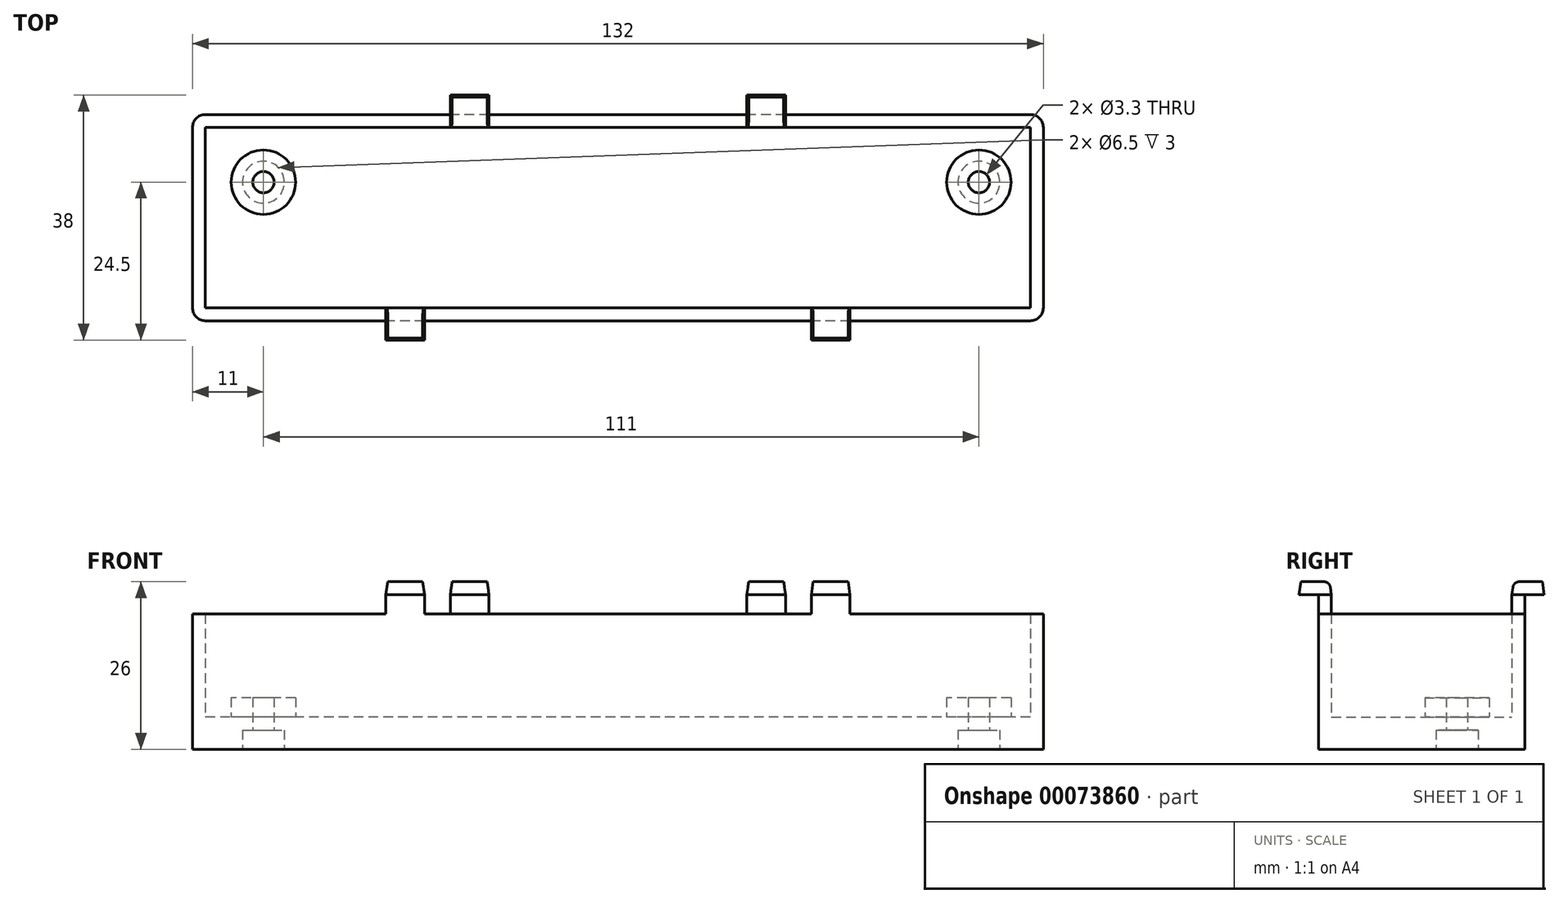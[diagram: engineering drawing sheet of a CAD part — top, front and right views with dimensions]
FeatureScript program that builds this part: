
annotation { "Feature Type Name" : "Feature", "Feature Type Description" : "" }
export const myFeature = defineFeature(function(context is Context, id is Id, definition is map)
    precondition{}
    {
        {
            var Q0;
            Q0=qCreatedBy(makeId("Top.planeOp"),FACE);
            var sketch = newSketch(context, id + "F0", { "sketchPlane" : qUnion([Q0])});
            skLineSegment(sketch, "E0.rect.bottom", {"start": v(64, -14) * mm, "end": v(-64, -14) * mm});
            skLineSegment(sketch, "E0.rect.top", {"start": v(64, 14) * mm, "end": v(-64, 14) * mm});
            skLineSegment(sketch, "E0.rect.left", {"start": v(64, -14) * mm, "end": v(64, 14) * mm});
            skLineSegment(sketch, "E0.rect.right", {"start": v(-64, -14) * mm, "end": v(-64, 14) * mm});
            skPoint(sketch, "E0.rect.middle", {"position": v(0, 0) * mm});
            skPoint(sketch, "E1", {"position": v(-55, 5.5) * mm});
            skPoint(sketch, "E2", {"position": v(56, 5.5) * mm});
            skCircle(sketch, "E3", {"center": v(-55, 5.5) * mm, "radius": 5 * mm});
            skCircle(sketch, "E4", {"center": v(56, 5.5) * mm, "radius": 5 * mm});
            skSolve(sketch);
        }
        {
            var Q0;
            Q0=makeQuery(id+"F0.imprint","IMPRINT",FACE,{"disambiguationData":[TD([[makeQuery(id+"F0.imprint","IMPRINT",EDGE,{"derivedFrom":sQuery(id+"F0.wireOp",EDGE,"E0.rect.bottom")}),-1.0]])]});
            var Q1;
            Q1=makeQuery(id+"F0.imprint","IMPRINT",FACE,{"disambiguationData":[TD([[makeQuery(id+"F0.imprint","IMPRINT",EDGE,{"derivedFrom":sQuery(id+"F0.wireOp",EDGE,"e8ff4094-02e6-4e03-b09e-d4d7426cd551")}),1.0]])]});
            var Q2;
            Q2=makeQuery(id+"F0.imprint","IMPRINT",FACE,{"disambiguationData":[TD([[makeQuery(id+"F0.imprint","IMPRINT",EDGE,{"derivedFrom":sQuery(id+"F0.wireOp",EDGE,"25a34238-af6a-4622-80d3-ac25b2c10ef1.0.startCap")}),-1.0]])]});
            var Q3;
            Q3=makeQuery(id+"F0.imprint","IMPRINT",FACE,{"disambiguationData":[TD([[makeQuery(id+"F0.imprint","IMPRINT",EDGE,{"derivedFrom":sQuery(id+"F0.wireOp",EDGE,"E3")}),1.0]])]});
            var Q4;
            Q4=makeQuery(id+"F0.imprint","IMPRINT",FACE,{"disambiguationData":[TD([[makeQuery(id+"F0.imprint","IMPRINT",EDGE,{"derivedFrom":sQuery(id+"F0.wireOp",EDGE,"E4")}),1.0]])]});
            var Q5;
            Q5=sQuery(id+"F0.wireOp",EDGE,"E0.rect.bottom");
            var Q6;
            Q6=sQuery(id+"F0.wireOp",EDGE,"E0.rect.right");
            var Q7;
            Q7=sQuery(id+"F0.wireOp",EDGE,"E0.rect.top");
            var Q8;
            Q8=sQuery(id+"F0.wireOp",EDGE,"E0.rect.left");
            extrude(context, id + "F1", {"entities" : qUnion([Q0, Q1, Q2, Q3, Q4]), "surfaceEntities" : qUnion([Q5, Q6, Q7, Q8]), "depth" : 16 * mm});
        }
        {
            var Q0;
            Q0=makeQuery(id+"F1.opExtrude","CAP_FACE",FACE,{"disambiguationData":[OSD([sQuery(id+"F0.wireOp",EDGE,"E0.rect.bottom"),sQuery(id+"F0.wireOp",EDGE,"E0.rect.top"),sQuery(id+"F0.wireOp",EDGE,"E0.rect.left"),sQuery(id+"F0.wireOp",EDGE,"E0.rect.right")])],"isStart":false});
            shell(context, id + "F2", {"entities" : qUnion([Q0]), "thickness" : 2 * mm, "oppositeDirection" : true});
        }
        {
            var Q0;
            Q0=makeQuery(id+"F1.opExtrude","CAP_FACE",FACE,{"disambiguationData":[OSD([sQuery(id+"F0.wireOp",EDGE,"E0.rect.bottom"),sQuery(id+"F0.wireOp",EDGE,"E0.rect.top"),sQuery(id+"F0.wireOp",EDGE,"E0.rect.left"),sQuery(id+"F0.wireOp",EDGE,"E0.rect.right")])],"isStart":false});
            var sketch = newSketch(context, id + "F3", { "sketchPlane" : qUnion([Q0])});
            skLineSegment(sketch, "E5", {"start": v(0, 24.52) * mm, "end": v(0, -22.95) * mm, "construction": true});
            skLineSegment(sketch, "E6.bottom", {"start": v(-26, 16) * mm, "end": v(-20, 16) * mm});
            skLineSegment(sketch, "E6.top", {"start": v(-26, 14) * mm, "end": v(-20, 14) * mm});
            skLineSegment(sketch, "E6.left", {"start": v(-26, 16) * mm, "end": v(-26, 14) * mm});
            skLineSegment(sketch, "E6.right", {"start": v(-20, 16) * mm, "end": v(-20, 14) * mm});
            skLineSegment(sketch, "E7.MirrorCS", {"start": v(26, 16) * mm, "end": v(20, 16) * mm});
            skLineSegment(sketch, "E8.MirrorCS", {"start": v(20, 16) * mm, "end": v(20, 14) * mm});
            skLineSegment(sketch, "E9.MirrorCS", {"start": v(26, 14) * mm, "end": v(20, 14) * mm});
            skLineSegment(sketch, "E10.MirrorCS", {"start": v(26, 16) * mm, "end": v(26, 14) * mm});
            skLineSegment(sketch, "E11.bottom", {"start": v(-36, -14) * mm, "end": v(-30, -14) * mm});
            skLineSegment(sketch, "E11.top", {"start": v(-36, -16) * mm, "end": v(-30, -16) * mm});
            skLineSegment(sketch, "E11.left", {"start": v(-36, -14) * mm, "end": v(-36, -16) * mm});
            skLineSegment(sketch, "E11.right", {"start": v(-30, -14) * mm, "end": v(-30, -16) * mm});
            skLineSegment(sketch, "E12.MirrorCS", {"start": v(30, -14) * mm, "end": v(30, -16) * mm});
            skLineSegment(sketch, "E13.MirrorCS", {"start": v(36, -14) * mm, "end": v(30, -14) * mm});
            skLineSegment(sketch, "E14.MirrorCS", {"start": v(36, -14) * mm, "end": v(36, -16) * mm});
            skLineSegment(sketch, "E15.MirrorCS", {"start": v(36, -16) * mm, "end": v(30, -16) * mm});
            skSolve(sketch);
        }
        {
            var Q0;
            Q0 = qSketchRegion(id + "F3", true);
            extrude(context, id + "F4", {"entities" : qUnion([Q0]), "operationType" : NewBodyOperationType.ADD, "depth" : 3 * mm});
        }
        {
            var Q0;
            Q0=makeQuery(id+"F4.opExtrude","CAP_FACE",FACE,{"disambiguationData":[OSD([sQuery(id+"F3.wireOp",EDGE,"E11.bottom"),sQuery(id+"F3.wireOp",EDGE,"E11.top"),sQuery(id+"F3.wireOp",EDGE,"E11.left"),sQuery(id+"F3.wireOp",EDGE,"E11.right")])],"isStart":false});
            var sketch = newSketch(context, id + "F5", { "sketchPlane" : qUnion([Q0])});
            skLineSegment(sketch, "E16.0", {"start": v(-26, 16) * mm, "end": v(-26, 14) * mm});
            skLineSegment(sketch, "E17.0", {"start": v(-26, 14) * mm, "end": v(-20, 14) * mm});
            skLineSegment(sketch, "E18.0", {"start": v(-20, 16) * mm, "end": v(-20, 14) * mm});
            skLineSegment(sketch, "E19.0", {"start": v(20, 16) * mm, "end": v(20, 14) * mm});
            skLineSegment(sketch, "E20.0", {"start": v(26, 14) * mm, "end": v(20, 14) * mm});
            skLineSegment(sketch, "E21.0", {"start": v(26, 16) * mm, "end": v(26, 14) * mm});
            skLineSegment(sketch, "E22.0", {"start": v(-36, -14) * mm, "end": v(-36, -16) * mm});
            skLineSegment(sketch, "E23.0", {"start": v(-36, -14) * mm, "end": v(-30, -14) * mm});
            skLineSegment(sketch, "E24.0", {"start": v(-30, -14) * mm, "end": v(-30, -16) * mm});
            skLineSegment(sketch, "E25.0", {"start": v(30, -14) * mm, "end": v(30, -16) * mm});
            skLineSegment(sketch, "E26.0", {"start": v(36, -14) * mm, "end": v(30, -14) * mm});
            skLineSegment(sketch, "E27.0", {"start": v(36, -14) * mm, "end": v(36, -16) * mm});
            skLineSegment(sketch, "E28", {"start": v(-26, 16) * mm, "end": v(-26, 19) * mm});
            skLineSegment(sketch, "E29", {"start": v(-26, 19) * mm, "end": v(-20, 19) * mm});
            skLineSegment(sketch, "E30", {"start": v(-20, 19) * mm, "end": v(-20, 16) * mm});
            skLineSegment(sketch, "E31.MirrorCS", {"start": v(26, 16) * mm, "end": v(26, 19) * mm});
            skLineSegment(sketch, "E32.MirrorCS", {"start": v(26, 19) * mm, "end": v(20, 19) * mm});
            skLineSegment(sketch, "E33.MirrorCS", {"start": v(20, 19) * mm, "end": v(20, 16) * mm});
            skLineSegment(sketch, "E34", {"start": v(-36, -16) * mm, "end": v(-36, -19) * mm});
            skLineSegment(sketch, "E35", {"start": v(-36, -19) * mm, "end": v(-30, -19) * mm});
            skLineSegment(sketch, "E36", {"start": v(-30, -19) * mm, "end": v(-30, -16) * mm});
            skLineSegment(sketch, "E37.MirrorCS", {"start": v(30, -19) * mm, "end": v(30, -16) * mm});
            skLineSegment(sketch, "E38.MirrorCS", {"start": v(36, -19) * mm, "end": v(30, -19) * mm});
            skLineSegment(sketch, "E39.MirrorCS", {"start": v(36, -16) * mm, "end": v(36, -19) * mm});
            skSolve(sketch);
        }
        {
            var Q0;
            Q0 = qSketchRegion(id + "F5", true);
            extrude(context, id + "F6", {"entities" : qUnion([Q0]), "operationType" : NewBodyOperationType.ADD, "depth" : 2 * mm, "hasDraft" : true, "draftAngle" : 8 * degree, "draftPullDirection" : true});
        }
        {
            var Q0;
            Q0=makeQuery(id+"F6.opExtrude","CAP_EDGE",EDGE,{"disambiguationData":[OSD([sQuery(id+"F5.wireOp",EDGE,"E26.0")])],"isStart":false});
            var Q1;
            Q1=makeQuery(id+"F6.opExtrude","CAP_EDGE",EDGE,{"disambiguationData":[OSD([sQuery(id+"F5.wireOp",EDGE,"E20.0")])],"isStart":false});
            var Q2;
            Q2=makeQuery(id+"F6.opExtrude","CAP_EDGE",EDGE,{"disambiguationData":[OSD([sQuery(id+"F5.wireOp",EDGE,"E17.0")])],"isStart":false});
            var Q3;
            Q3=makeQuery(id+"F6.opExtrude","CAP_EDGE",EDGE,{"disambiguationData":[OSD([sQuery(id+"F5.wireOp",EDGE,"E23.0")])],"isStart":false});
            fillet(context, id + "F7", {"entities" : qUnion([Q0, Q1, Q2, Q3]), "radius" : 1 * mm, "tangentPropagation" : true, "allowEdgeOverflow" : false});
        }
        {
            var Q0;
            Q0=makeQuery(id+"F1.opExtrude","SWEPT_EDGE",EDGE,{"disambiguationData":[OSD([sQuery(id+"F0.wireOp",EDGE,"E0.rect.bottom"),sQuery(id+"F0.wireOp",EDGE,"E0.rect.right")])]});
            var Q1;
            Q1=makeQuery(id+"F1.opExtrude","SWEPT_EDGE",EDGE,{"disambiguationData":[OSD([sQuery(id+"F0.wireOp",EDGE,"E0.rect.top"),sQuery(id+"F0.wireOp",EDGE,"E0.rect.right")])]});
            var Q2;
            Q2=makeQuery(id+"F1.opExtrude","SWEPT_EDGE",EDGE,{"disambiguationData":[OSD([sQuery(id+"F0.wireOp",EDGE,"E0.rect.bottom"),sQuery(id+"F0.wireOp",EDGE,"E0.rect.left")])]});
            var Q3;
            Q3=makeQuery(id+"F1.opExtrude","SWEPT_EDGE",EDGE,{"disambiguationData":[OSD([sQuery(id+"F0.wireOp",EDGE,"E0.rect.top"),sQuery(id+"F0.wireOp",EDGE,"E0.rect.left")])]});
            fillet(context, id + "F8", {"entities" : qUnion([Q0, Q1, Q2, Q3]), "radius" : 2 * mm, "tangentPropagation" : true, "allowEdgeOverflow" : false});
        }
        {
            var Q0;
            Q0=makeQuery(id+"F1.opExtrude","CAP_FACE",FACE,{"disambiguationData":[OSD([sQuery(id+"F0.wireOp",EDGE,"E0.rect.bottom"),sQuery(id+"F0.wireOp",EDGE,"E0.rect.top"),sQuery(id+"F0.wireOp",EDGE,"E0.rect.left"),sQuery(id+"F0.wireOp",EDGE,"E0.rect.right")])],"isStart":true});
            extrude(context, id + "F9", {"entities" : qUnion([Q0]), "operationType" : NewBodyOperationType.ADD, "depth" : 3 * mm});
        }
        {
            var Q0;
            Q0=makeQuery(id+"F0.imprint","IMPRINT",FACE,{"disambiguationData":[TD([[makeQuery(id+"F0.imprint","IMPRINT",EDGE,{"derivedFrom":sQuery(id+"F0.wireOp",EDGE,"E3")}),1.0]])]});
            var Q1;
            Q1=makeQuery(id+"F0.imprint","IMPRINT",FACE,{"disambiguationData":[TD([[makeQuery(id+"F0.imprint","IMPRINT",EDGE,{"derivedFrom":sQuery(id+"F0.wireOp",EDGE,"E4")}),1.0]])]});
            extrude(context, id + "F10", {"entities" : qUnion([Q0, Q1]), "operationType" : NewBodyOperationType.ADD, "depth" : 3 * mm});
        }
        {
            var Q0;
            Q0=makeQuery(id+"F9.opExtrude","CAP_FACE",FACE,{"disambiguationData":[OSD([sQuery(id+"F0.wireOp",EDGE,"E0.rect.bottom"),sQuery(id+"F0.wireOp",EDGE,"E0.rect.top"),sQuery(id+"F0.wireOp",EDGE,"E0.rect.left"),sQuery(id+"F0.wireOp",EDGE,"E0.rect.right")])],"isStart":false});
            var sketch = newSketch(context, id + "F11", { "sketchPlane" : qUnion([Q0])});
            skPoint(sketch, "E40.0", {"position": v(56, -5.5) * mm});
            skPoint(sketch, "E40.1", {"position": v(-55, -5.5) * mm});
            skSolve(sketch);
        }
        {
            var Q0;
            Q0=sQuery(id+"F11.wireOp",VERTEX,"E40.0");
            var Q1;
            Q1=sQuery(id+"F11.wireOp",VERTEX,"E40.1");
            var Q2;
            Q2=makeQuery(id+"F1.opExtrude","SWEPT_BODY",BODY,{"disambiguationData":[OSD([sQuery(id+"F0.wireOp",EDGE,"E0.rect.bottom"),sQuery(id+"F0.wireOp",EDGE,"E0.rect.top"),sQuery(id+"F0.wireOp",EDGE,"E0.rect.left"),sQuery(id+"F0.wireOp",EDGE,"E0.rect.right")])]});
            hole(context, id + "F12", {"style" : HoleStyle.C_BORE, "endStyle" : HoleEndStyle.THROUGH, "standardTappedOrClearance" : lookupTablePath({ "standard" : "ISO", "fit" : "Normal", "size" : "M3", "type" : "Clearance" }), "standardBlindInLast" : lookupTablePath({ "fit" : "Standard", "standard" : "ISO", "size" : "M3", "type" : "Clearance" }), "holeDiameter" : 3.3 * mm, "cBoreDiameter" : 6.5 * mm, "cBoreDepth" : 3 * mm, "locations" : qUnion([Q0, Q1]), "scope" : qUnion([Q2]), "isTappedThrough" : true});
        }
    });
